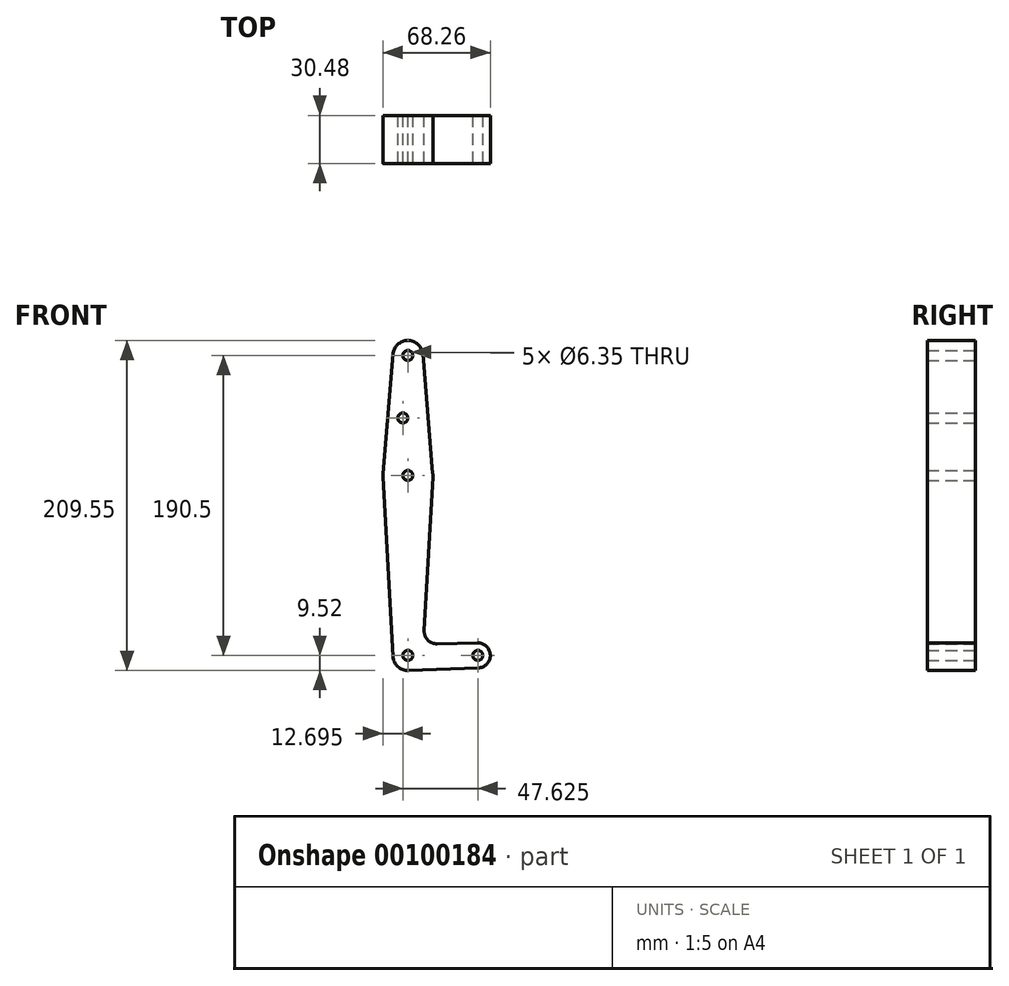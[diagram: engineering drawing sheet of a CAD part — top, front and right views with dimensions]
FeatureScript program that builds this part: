
annotation { "Feature Type Name" : "Feature", "Feature Type Description" : "" }
export const myFeature = defineFeature(function(context is Context, id is Id, definition is map)
    precondition{}
    {
        {
            var Q0;
            Q0=qCreatedBy(makeId("Front.planeOp"),FACE);
            var sketch = newSketch(context, id + "F0", { "sketchPlane" : qUnion([Q0])});
            skCircle(sketch, "E0", {"center": v(0, 0) * mm, "radius": 9.53 * mm});
            skCircle(sketch, "E1", {"center": v(0, 190.5) * mm, "radius": 9.53 * mm});
            skCircle(sketch, "E2", {"center": v(0, 114.3) * mm, "radius": 15.88 * mm});
            skCircle(sketch, "E3", {"center": v(44.45, 0) * mm, "radius": 7.94 * mm});
            skLineSegment(sketch, "E4", {"start": v(0, 190.5) * mm, "end": v(0, 114.3) * mm, "construction": true});
            skLineSegment(sketch, "E5", {"start": v(0, 114.3) * mm, "end": v(0, 0) * mm, "construction": true});
            skLineSegment(sketch, "E6", {"start": v(0, 0) * mm, "end": v(44.45, 0) * mm, "construction": true});
            skLineSegment(sketch, "E7", {"start": v(15.85, 113.42) * mm, "end": v(10.42, 15.81) * mm});
            skLineSegment(sketch, "E8", {"start": v(18.52, 7.42) * mm, "end": v(44.3, 7.94) * mm});
            skLineSegment(sketch, "E9", {"start": v(0.34, -9.52) * mm, "end": v(44.73, -7.93) * mm});
            skLineSegment(sketch, "E10", {"start": v(-15.85, 113.42) * mm, "end": v(-9.51, -0.53) * mm});
            skLineSegment(sketch, "E11", {"start": v(-15.82, 115.62) * mm, "end": v(-9.5, 191.3) * mm});
            skLineSegment(sketch, "E12", {"start": v(9.5, 191.3) * mm, "end": v(15.82, 115.62) * mm});
            skCircle(sketch, "E13", {"center": v(0, 190.5) * mm, "radius": 3.18 * mm});
            skCircle(sketch, "E14", {"center": v(0, 114.3) * mm, "radius": 3.18 * mm});
            skCircle(sketch, "E15", {"center": v(0, 0) * mm, "radius": 3.18 * mm});
            skCircle(sketch, "E16", {"center": v(44.45, 0) * mm, "radius": 3.18 * mm});
            skCircle(sketch, "E17", {"center": v(-3.18, 150.83) * mm, "radius": 3.18 * mm});
            skArc(sketch, "E18.filletArc", {"start": v(10.42, 15.81) * mm, "mid": v(12.64, 9.85) * mm, "end": v(18.52, 7.42) * mm});
            skSolve(sketch);
        }
        {
            var Q0;
            Q0 = qSketchRegion(id + "F0", true);
            extrude(context, id + "F1", {"entities" : qUnion([Q0]), "depth" : 30.48 * mm});
        }
    });
